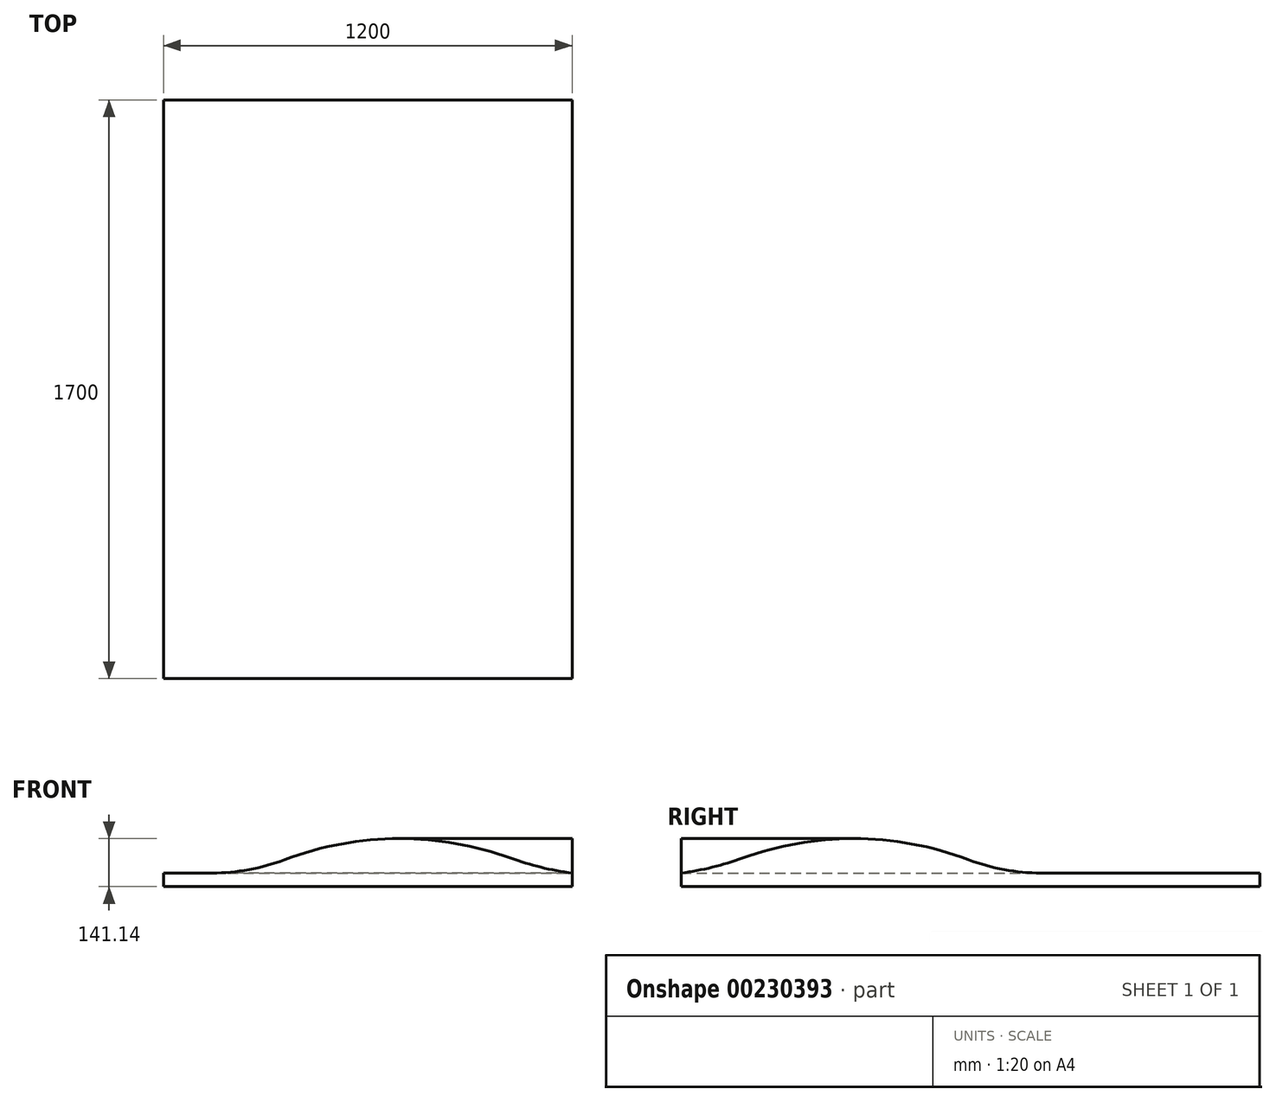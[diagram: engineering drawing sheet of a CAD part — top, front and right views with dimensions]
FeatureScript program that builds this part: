
annotation { "Feature Type Name" : "Feature", "Feature Type Description" : "" }
export const myFeature = defineFeature(function(context is Context, id is Id, definition is map)
    precondition{}
    {
        {
            var Q0;
            Q0=qCreatedBy(makeId("Top.planeOp"),FACE);
            var sketch = newSketch(context, id + "F0", { "sketchPlane" : qUnion([Q0])});
            skLineSegment(sketch, "E0.bottom", {"start": v(600, -850) * mm, "end": v(-600, -850) * mm});
            skLineSegment(sketch, "E0.top", {"start": v(600, 850) * mm, "end": v(-600, 850) * mm});
            skLineSegment(sketch, "E0.left", {"start": v(600, -850) * mm, "end": v(600, 850) * mm});
            skLineSegment(sketch, "E0.right", {"start": v(-600, -850) * mm, "end": v(-600, 850) * mm});
            skPoint(sketch, "E0.middle", {"position": v(0, 0) * mm});
            skSolve(sketch);
        }
        {
            var Q0;
            Q0=makeQuery(id+"F0.imprint","IMPRINT",FACE,{"disambiguationData":[TD([[makeQuery(id+"F0.imprint","IMPRINT",EDGE,{"derivedFrom":sQuery(id+"F0.wireOp",EDGE,"E0.bottom")}),-1.0]])]});
            extrude(context, id + "F1", {"entities" : qUnion([Q0]), "depth" : 40 * mm});
        }
        {
            var Q0;
            Q0=makeQuery(id+"F1.opExtrude","CAP_FACE",FACE,{"disambiguationData":[OSD([sQuery(id+"F0.wireOp",EDGE,"E0.bottom"),sQuery(id+"F0.wireOp",EDGE,"E0.top"),sQuery(id+"F0.wireOp",EDGE,"E0.left"),sQuery(id+"F0.wireOp",EDGE,"E0.right")])],"isStart":false});
            var sketch = newSketch(context, id + "F2", { "sketchPlane" : qUnion([Q0])});
            skArc(sketch, "E1", {"start": v(600, 207.13) * mm, "mid": v(-147.5, -102.5) * mm, "end": v(-457.13, -850) * mm});
            skSolve(sketch);
        }
        {
            var Q0;
            Q0=makeQuery(id+"F1.opExtrude","SWEPT_FACE",FACE,{"disambiguationData":[OSD([sQuery(id+"F0.wireOp",EDGE,"E0.bottom")])]});
            var sketch = newSketch(context, id + "F3", { "sketchPlane" : qUnion([Q0])});
            skLineSegment(sketch, "E2.0", {"start": v(600, 40) * mm, "end": v(-457.13, 40) * mm});
            skLineSegment(sketch, "E3", {"start": v(0, 40) * mm, "end": v(0, 190) * mm, "construction": true});
            skPoint(sketch, "E3.endSnap0", {"position": v(0, 40) * mm});
            skArc(sketch, "E4", {"start": v(-457.13, 40) * mm, "mid": v(-348.84, 49.85) * mm, "end": v(-244.11, 79.09) * mm});
            skArc(sketch, "E5", {"start": v(419.14, 83.94) * mm, "mid": v(87.08, 141.11) * mm, "end": v(-244.11, 79.09) * mm});
            skArc(sketch, "E6", {"start": v(419.14, 83.94) * mm, "mid": v(508.36, 56.99) * mm, "end": v(600, 40) * mm});
            skSolve(sketch);
        }
        {
            var Q0;
            Q0=makeQuery(id+"F3.imprint","IMPRINT",FACE,{"disambiguationData":[TD([[makeQuery(id+"F3.imprint","IMPRINT",EDGE,{"derivedFrom":sQuery(id+"F3.wireOp",EDGE,"E2.0")}),-1.0]])]});
            var Q1;
            Q1=sQuery(id+"F2.wireOp",EDGE,"E1");
            sweep(context, id + "F4", {"operationType" : NewBodyOperationType.ADD, "profiles" : qUnion([Q0]), "path" : qUnion([Q1])});
        }
    });
